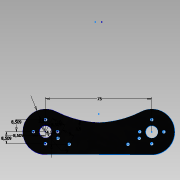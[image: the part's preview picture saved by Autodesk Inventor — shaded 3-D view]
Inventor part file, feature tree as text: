
AUTODESK INVENTOR PART (.ipt)
format: ipt  version: 2015 SP1 (Build 190203100, 203)  size: 131,072 bytes
history: native  units: mm
features: extrude x2, sketch x1
ambient origin geometry x8: Origin, YZ Plane, XZ Plane, XY Plane, X Axis, Y Axis, Z Axis, Center Point
bodies: Body1 (feature_tree)
feature tree (3):
  sketch  "Sketch1"  dims[d47=8.509mm d48=8.509mm d49=8.509mm d50=8.509mm d51=10.0mm d53=9.0mm d56=9.0mm d58=4.19811mm d61=75.0mm d62=7.0mm d63=0.0mm d67=3.5mm d68=3.5mm d69=7.0mm d70=0.0mm]
  extrude  "Extrusion3"  Depth=7.0mm
  extrude  "Extrusion4"  Depth=7.0mm
